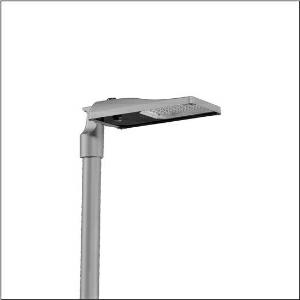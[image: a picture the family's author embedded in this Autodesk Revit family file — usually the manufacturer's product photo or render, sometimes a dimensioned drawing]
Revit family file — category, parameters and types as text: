
# Revit family: streetlight_sl_31_mini___st1_0a_5xh6d31t08ja_9cd4
name_source: partatom
category: Lighting Fixtures
units: mm (PartAtom-declared; Revit-internal decimal feet)

## family parameters
Cut with Voids When Loaded = No
Host = Face
Light Source = No
Part Type = Normal
Room Calculation Point = No
Round Connector Dimension = Use Diameter
Shared = No

## types (1)
- --- (1 x LED, 12270 lm, 82.5 W, 3000K)
    Apparent Load = 83 VA
    CIE Flux Codes = 40 73 97 100 100
    Color Rendering = 70
    Color Temperature = 3000K
    Default Elevation = 1800 mm
    Description = Streetlight SL 31 mini D4i, Desk-Remote mast luminaire for post-top, side-entry; light control with lens of PMMA; light distribution: ST1.0a, direct asymmetric distribution, for standard-compliant lighting for roads and squares; LED: luminous flux: 12.270lm, light colour: 730, colour temperature: 3000K; luminous efficacy: 148,7lm/W; control: pre-setting: logarithmic dimming characteristic, flexible luminous flux parameterisation, time-dependent luminous flux control, constant luminous flux control, power reduction, intelligent temperature release in ECG and LED module, overheat protection; luminaire housing, of diecast aluminium, SITECO metallic grey (DB 702S), corrosivity category C5 high according to DIN EN ISO 12944; cover of toughened safety glass, transparent, opened without tools; mast flange of diecast aluminium, SITECO metallic grey (DB 702S), spigot size: 76/60mm, mast flange included unmounted; cable length: 10,5m, connection cable pre-assembled; mains connection: 220..240V, AC, 50/60Hz; power consumption (at start of service life): 82,5W / (at end of service life): 90,1W / (with reduced operation 50%): 36,8W; protection rating (complete): IP66; insulation class (complete): insulation class II (safety insulation); impact resistance: IK09; certification: CE, ENEC, ENEC+, VDE, UKCA, ZD4i; permissible operating ambient temperature for outdoor applications: -40..+50°C; packaging unit: 1 piece

Light Distribution: ST1.0a
    Height = 76 mm
    Lamp = 1 x LED
    Lamp Light Flux = 12270 lm
    Lamp Power = 82.5 W
    Lamp count = 1
    Length = 547 mm
    Luminous efficacy = 149 lm/W
    Manufacturer = Siteco
    ModVariant = No
    Model = 5XH6D31T08JA
    Number of Poles = 1
    OnlyDefault = Yes
    Power Factor = 1
    Product Name = Streetlight SL 31 mini | ST1.0a
    Product group = mast luminaire | pylon top
    ProductGroupID = 6100
    Protection Class = Protection class II
    Protection Degree = IP 66
    RLX_Detail_Level = 1
    RLX_Emergency_Light_Flux = 0 lm
    RLX_Emergency_Type = 0
    RLX_Emergency_Type_DB = No
    RlxData = <blob elided: 39857 chars, md5=a88fed74>
    Socket = socket
    Standby Power = 0 W
    System Light Flux = 12270 lm
    System Power = 83 W
    Type Comments = factory setting: luminous flux: 100 % | dim-lin: 254 | 870 mA
    Type Image = l_1300332.jpg
    URL = http://relux.com
    VarID = @adj_057075
    Voltage = 0 V
    Weight = 0.00 kg
    Width = 265 mm

## geometry (parser evidence)
native form markers: Blend x4, Sweep x12
no freeform markers — native parametric forms only
